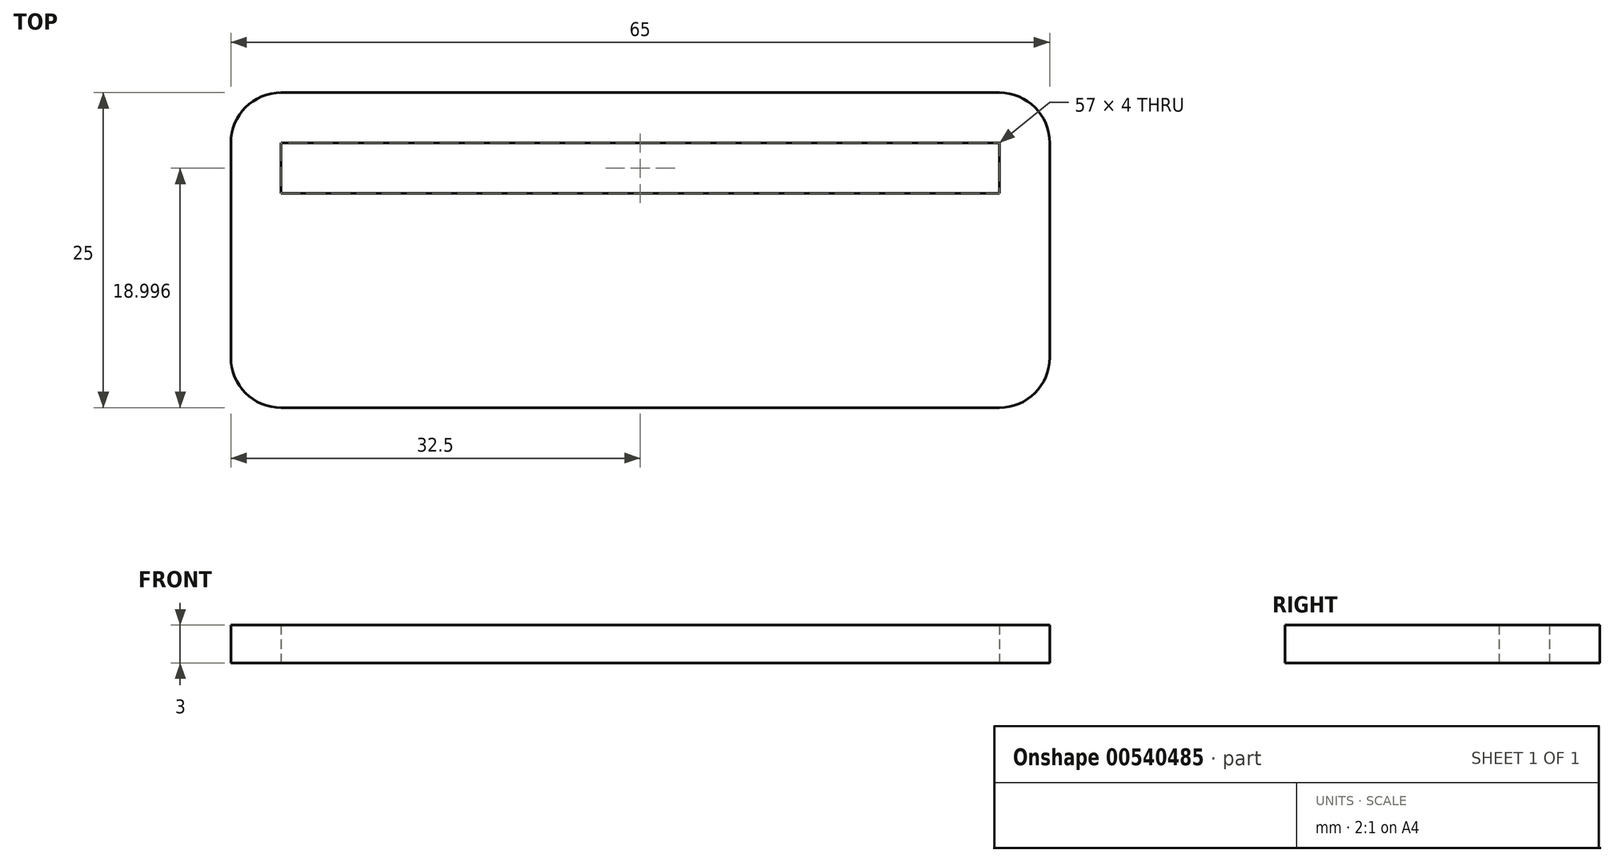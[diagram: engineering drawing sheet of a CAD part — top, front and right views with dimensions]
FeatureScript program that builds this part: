
annotation { "Feature Type Name" : "Feature", "Feature Type Description" : "" }
export const myFeature = defineFeature(function(context is Context, id is Id, definition is map)
    precondition{}
    {
        {
            var Q0;
            Q0=qCreatedBy(makeId("Top.planeOp"),FACE);
            var sketch = newSketch(context, id + "F0", { "sketchPlane" : qUnion([Q0])});
            skLineSegment(sketch, "E0.bottom", {"start": v(-23.85, 7.06) * mm, "end": v(41.15, 7.06) * mm});
            skLineSegment(sketch, "E0.top", {"start": v(-23.85, -17.94) * mm, "end": v(41.15, -17.94) * mm});
            skLineSegment(sketch, "E0.left", {"start": v(-23.85, 7.06) * mm, "end": v(-23.85, -17.94) * mm});
            skLineSegment(sketch, "E0.right", {"start": v(41.15, 7.06) * mm, "end": v(41.15, -17.94) * mm});
            skLineSegment(sketch, "E1.bottom", {"start": v(-19.85, 3.06) * mm, "end": v(37.15, 3.06) * mm});
            skLineSegment(sketch, "E1.top", {"start": v(-19.85, -0.94) * mm, "end": v(37.15, -0.94) * mm});
            skLineSegment(sketch, "E1.left", {"start": v(-19.85, 3.06) * mm, "end": v(-19.85, -0.94) * mm});
            skLineSegment(sketch, "E1.right", {"start": v(37.15, 3.06) * mm, "end": v(37.15, -0.94) * mm});
            skSolve(sketch);
        }
        {
            var Q0;
            Q0 = qSketchRegion(id + "F0", true);
            extrude(context, id + "F1", {"entities" : qUnion([Q0]), "depth" : 3 * mm, "offsetDistance" : 25 * mm});
        }
        {
            var Q0;
            Q0=makeQuery(id+"F1.opExtrude","SWEPT_EDGE",EDGE,{"disambiguationData":[OSD([sQuery(id+"F0.wireOp",EDGE,"E0.top"),sQuery(id+"F0.wireOp",EDGE,"E0.left")])]});
            var Q1;
            Q1=makeQuery(id+"F1.opExtrude","SWEPT_EDGE",EDGE,{"disambiguationData":[OSD([sQuery(id+"F0.wireOp",EDGE,"E0.top"),sQuery(id+"F0.wireOp",EDGE,"E0.right")])]});
            var Q2;
            Q2=makeQuery(id+"F1.opExtrude","SWEPT_EDGE",EDGE,{"disambiguationData":[OSD([sQuery(id+"F0.wireOp",EDGE,"E0.bottom"),sQuery(id+"F0.wireOp",EDGE,"E0.left")])]});
            var Q3;
            Q3=makeQuery(id+"F1.opExtrude","SWEPT_EDGE",EDGE,{"disambiguationData":[OSD([sQuery(id+"F0.wireOp",EDGE,"E0.bottom"),sQuery(id+"F0.wireOp",EDGE,"E0.right")])]});
            fillet(context, id + "F2", {"entities" : qUnion([Q0, Q1, Q2, Q3]), "radius" : 4 * mm, "tangentPropagation" : true, "allowEdgeOverflow" : false});
        }
    });
